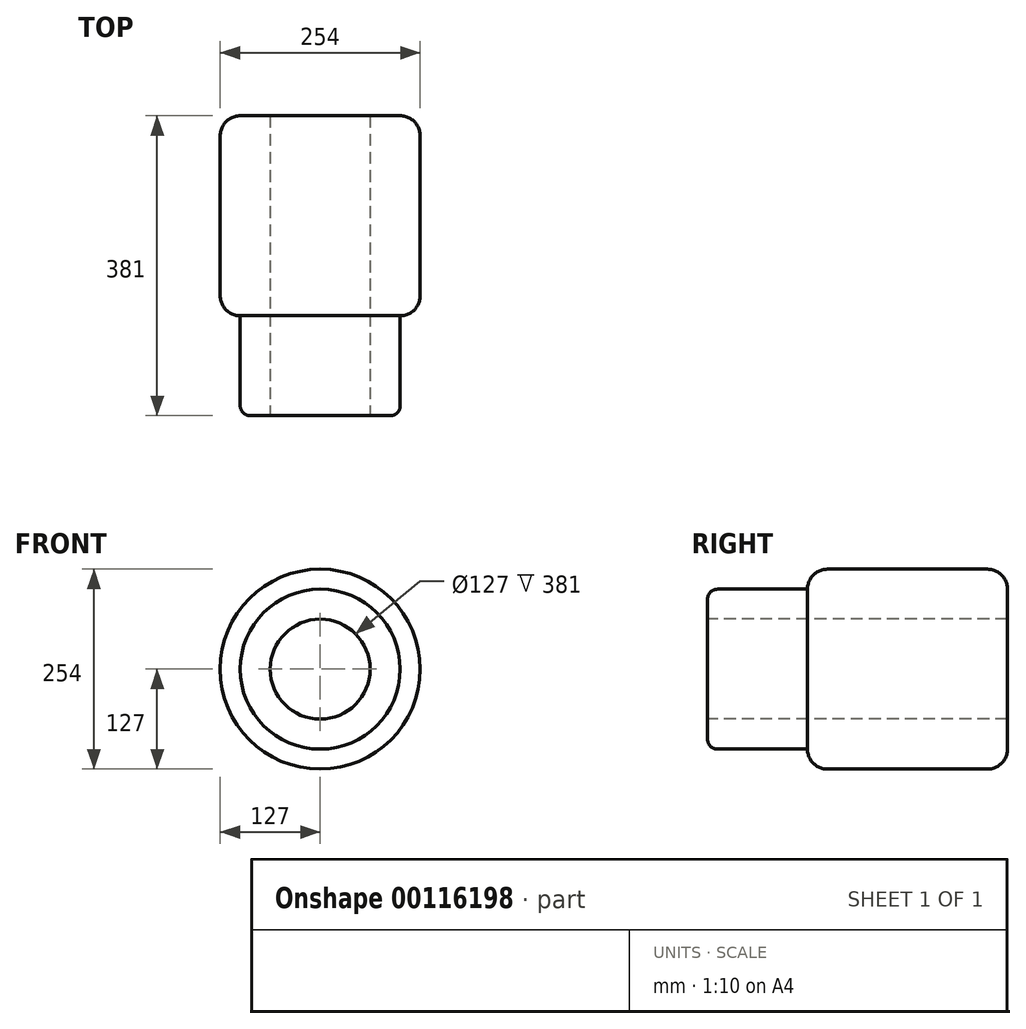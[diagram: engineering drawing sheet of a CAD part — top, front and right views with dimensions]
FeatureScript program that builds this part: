
annotation { "Feature Type Name" : "Feature", "Feature Type Description" : "" }
export const myFeature = defineFeature(function(context is Context, id is Id, definition is map)
    precondition{}
    {
        {
            var Q0;
            Q0=qCreatedBy(makeId("Front.planeOp"),FACE);
            var sketch = newSketch(context, id + "F0", { "sketchPlane" : qUnion([Q0])});
            skCircle(sketch, "E0", {"center": v(0, 0) * mm, "radius": 127 * mm});
            skSolve(sketch);
        }
        {
            var Q0;
            Q0 = qSketchRegion(id + "F0", true);
            extrude(context, id + "F1", {"entities" : qUnion([Q0]), "depth" : 254 * mm});
        }
        {
            var Q0;
            Q0=makeQuery(id+"F1.opExtrude","CAP_EDGE",EDGE,{"disambiguationData":[OSD([sQuery(id+"F0.wireOp",EDGE,"E0")])],"isStart":false});
            var Q1;
            Q1=makeQuery(id+"F1.opExtrude","CAP_EDGE",EDGE,{"disambiguationData":[OSD([sQuery(id+"F0.wireOp",EDGE,"E0")])],"isStart":true});
            fillet(context, id + "F2", {"entities" : qUnion([Q0, Q1]), "radius" : 25.4 * mm, "tangentPropagation" : true, "allowEdgeOverflow" : false});
        }
        {
            var Q0;
            Q0=makeQuery(id+"F1.opExtrude","CAP_FACE",FACE,{"disambiguationData":[OSD([sQuery(id+"F0.wireOp",EDGE,"E0")])],"isStart":false});
            var sketch = newSketch(context, id + "F3", { "sketchPlane" : qUnion([Q0])});
            skPoint(sketch, "E1", {"position": v(0, 0) * mm});
            skSolve(sketch);
        }
        {
            var Q0;
            Q0=sQuery(id+"F3.wireOp",VERTEX,"E1");
            var Q1;
            Q1=makeQuery(id+"F1.opExtrude","SWEPT_BODY",BODY,{"disambiguationData":[OSD([sQuery(id+"F0.wireOp",EDGE,"E0")])]});
            hole(context, id + "F4", {"style" : HoleStyle.SIMPLE, "endStyle" : HoleEndStyle.THROUGH, "holeDiameter" : 127 * mm, "locations" : qUnion([Q0]), "scope" : qUnion([Q1]), "isTappedThrough" : true});
        }
        {
            var Q0;
            Q0=makeQuery(id+"F1.opExtrude","CAP_FACE",FACE,{"disambiguationData":[OSD([sQuery(id+"F0.wireOp",EDGE,"E0")])],"isStart":false});
            extrude(context, id + "F5", {"entities" : qUnion([Q0]), "operationType" : NewBodyOperationType.ADD, "depth" : 127 * mm});
        }
        {
            var Q0;
            Q0=makeQuery(id+"F5.opExtrude","CAP_EDGE",EDGE,{"disambiguationData":[OSD([sQuery(id+"F0.wireOp",EDGE,"E0")])],"isStart":false});
            var Q1;
            Q1=makeQuery(id+"F5.opExtrude","CAP_EDGE",EDGE,{"disambiguationData":[OSD([sQuery(id+"F4.hole-0.sketch.wireOp",EDGE,"core_line_2"),sQuery(id+"F4.hole-0.sketch.wireOp",EDGE,"core_line_3")])],"isStart":false});
            fillet(context, id + "F6", {"entities" : qUnion([Q0, Q1]), "radius" : 12.7 * mm, "tangentPropagation" : true, "allowEdgeOverflow" : false});
        }
    });
